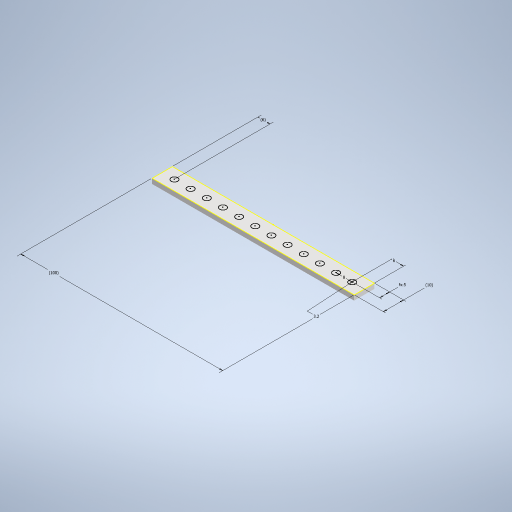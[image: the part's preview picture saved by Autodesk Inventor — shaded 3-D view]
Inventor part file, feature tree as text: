
AUTODESK INVENTOR PART (.ipt)
format: ipt  version: 2024.1 (Build 281209000, 209)  size: 254,464 bytes
history: native  units: mm
features: sketch x2, extrude x1
ambient origin geometry x8: Origin, YZ Plane, XZ Plane, XY Plane, X Axis, Y Axis, Z Axis, Center Point
bodies: Solid1 (feature_tree)
feature tree (3):
  extrude  "Extrusion1"  Depth=100.0mm
  sketch  "Sketch2"  dims[d2=50.0mm d3=2.5mm d4=0.0mm d5=6.0mm d6=3.2mm d7=10.0mm d8=5.0mm d10=100.0mm d11=120.0mm d13=8.0mm d14=10.0mm d16=10.0mm d18=6.0mm]
  sketch  "Sketch1"  dims[d0=10.0mm d1=100.0mm]
